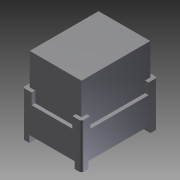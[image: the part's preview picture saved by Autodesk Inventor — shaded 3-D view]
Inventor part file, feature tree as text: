
AUTODESK INVENTOR PART (.ipt)
format: ipt  version: 2011 SP1 (Build 150282100, 282)  size: 159,744 bytes
history: native  units: in
note: dims shown in document units (in); Inventor stores cm internally (conversion verified against a paired STEP export)
features: other x42, extrude x9, sketch x9
ambient origin geometry x8: Origin, YZ Plane, XZ Plane, XY Plane, X Axis, Y Axis, Z Axis, Center Point
bodies: Solid1 (feature_tree)
feature tree (60):
  extrude  "Extrusion1"  Depth=0.144in TaperAngle=0.0deg
  extrude  "Extrusion2"  Depth=0.346in TaperAngle=0.0deg
  extrude  "Extrusion3"  Depth=0.016in TaperAngle=0.0deg
  extrude  "Extrusion4"  Depth=0.016in TaperAngle=0.0deg
  extrude  "Extrusion5"  [1 undecoded]
  extrude  "Extrusion6"  [1 undecoded]
  extrude  "Extrusion7"  [1 undecoded]
  extrude  "Extrusion8"  [1 undecoded]
  extrude  "Extrusion9"  [1 undecoded]
  other  "black_body_str_XY"
  other  "black_body_str_YZ"
  other  "black_body_str_ZX"
  other  "black_body_str_X"
  other  "black_body_str_Y"
  other  "black_body_str_Z"
  other  "black_body_str_Center"
  other  "black_body_ver_rigang_XY"
  other  "black_body_ver_rigang_YZ"
  other  "black_body_ver_rigang_ZX"
  other  "black_body_ver_rigang_X"
  other  "black_body_ver_rigang_Y"
  other  "black_body_ver_rigang_Z"
  other  "black_body_ver_rigang_Center"
  other  "dummy_righ_vert_XY"
  other  "dummy_righ_vert_YZ"
  other  "dummy_righ_vert_ZX"
  other  "dummy_righ_vert_X"
  other  "dummy_righ_vert_Y"
  other  "dummy_righ_vert_Z"
  other  "dummy_righ_vert_Center"
  other  "dummy_straight_XY"
  other  "dummy_straight_YZ"
  other  "dummy_straight_ZX"
  other  "dummy_straight_X"
  other  "dummy_straight_Y"
  other  "dummy_straight_Z"
  other  "dummy_straight_Center"
  other  "rigang_vert_trmnls_XY"
  other  "rigang_vert_trmnls_YZ"
  other  "rigang_vert_trmnls_ZX"
  other  "rigang_vert_trmnls_X"
  other  "rigang_vert_trmnls_Y"
  other  "rigang_vert_trmnls_Z"
  other  "rigang_vert_trmnls_Center"
  other  "str_trmnls_XY"
  other  "str_trmnls_YZ"
  other  "str_trmnls_ZX"
  other  "str_trmnls_X"
  other  "str_trmnls_Y"
  other  "str_trmnls_Z"
  other  "str_trmnls_Center"
  sketch  "Sketch_1"  dims[d0=0.348in d1=0.0in d2=0.144in d3=0.0in]
  sketch  "Sketch_2"  dims[d4=0.268in d5=0.0in d6=0.346in d7=0.0in]
  sketch  "Sketch_3"  dims[d8=0.016in d9=0.0in d10=0.016in d11=0.0in]
  sketch  "Sketch_4"  dims[d12=0.016in d13=0.0in d14=0.016in d15=0.0in]
  sketch  "Sketch_5"  dims[d16=0.001in d17=0.0in]
  sketch  "Sketch_6"
  sketch  "Sketch_7"
  sketch  "Sketch_8"
  sketch  "Sketch_49"
note: 5 required parameter values undecoded (feature->parameter linkage not recoverable at this tier; creation-order binding heuristic only, values carry confidence <= 0.55)
